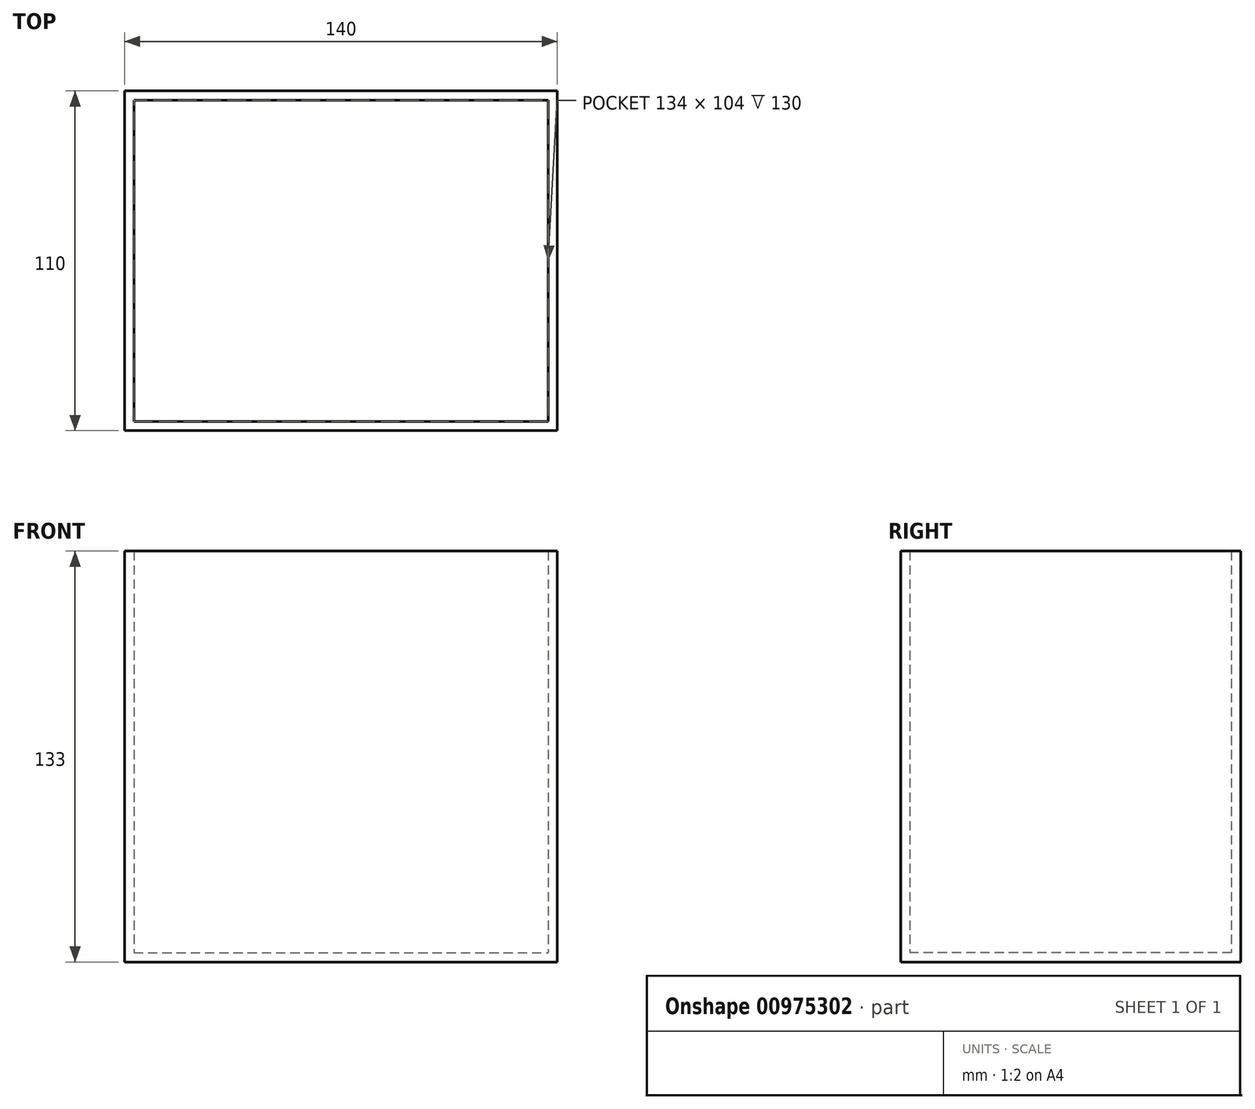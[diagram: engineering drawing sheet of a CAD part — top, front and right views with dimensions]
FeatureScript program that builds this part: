
annotation { "Feature Type Name" : "Feature", "Feature Type Description" : "" }
export const myFeature = defineFeature(function(context is Context, id is Id, definition is map)
    precondition{}
    {
        {
            var Q0;
            Q0=qCreatedBy(makeId("Top.planeOp"),FACE);
            var sketch = newSketch(context, id + "F0", { "sketchPlane" : qUnion([Q0])});
            skLineSegment(sketch, "E0.bottom", {"start": v(-70, 55) * mm, "end": v(70, 55) * mm});
            skLineSegment(sketch, "E0.top", {"start": v(-70, -55) * mm, "end": v(70, -55) * mm});
            skLineSegment(sketch, "E0.left", {"start": v(-70, 55) * mm, "end": v(-70, -55) * mm});
            skLineSegment(sketch, "E0.right", {"start": v(70, 55) * mm, "end": v(70, -55) * mm});
            skLineSegment(sketch, "E1.bottom", {"start": v(-67, 52) * mm, "end": v(67, 52) * mm});
            skLineSegment(sketch, "E1.top", {"start": v(-67, -52) * mm, "end": v(67, -52) * mm});
            skLineSegment(sketch, "E1.left", {"start": v(-67, 52) * mm, "end": v(-67, -52) * mm});
            skLineSegment(sketch, "E1.right", {"start": v(67, 52) * mm, "end": v(67, -52) * mm});
            skSolve(sketch);
        }
        {
            var Q0;
            Q0=makeQuery(id+"F0.imprint","IMPRINT",FACE,{"disambiguationData":[TD([[makeQuery(id+"F0.imprint","IMPRINT",EDGE,{"derivedFrom":sQuery(id+"F0.wireOp",EDGE,"E0.bottom")}),-1.0]])]});
            extrude(context, id + "F1", {"entities" : qUnion([Q0]), "depth" : 130 * mm, "offsetDistance" : 25 * mm});
        }
        {
            var Q0;
            Q0=qCreatedBy(makeId("Top.planeOp"),FACE);
            var sketch = newSketch(context, id + "F2", { "sketchPlane" : qUnion([Q0])});
            skLineSegment(sketch, "E2.0", {"start": v(-70, -55) * mm, "end": v(70, -55) * mm});
            skLineSegment(sketch, "E3.0", {"start": v(-70, 55) * mm, "end": v(-70, -55) * mm});
            skLineSegment(sketch, "E4.0", {"start": v(70, 55) * mm, "end": v(70, -55) * mm});
            skLineSegment(sketch, "E5.0", {"start": v(-70, 55) * mm, "end": v(70, 55) * mm});
            skSolve(sketch);
        }
        {
            var Q0;
            Q0 = qSketchRegion(id + "F2", true);
            extrude(context, id + "F3", {"entities" : qUnion([Q0]), "operationType" : NewBodyOperationType.ADD, "oppositeDirection" : true, "depth" : 3 * mm, "offsetDistance" : 25 * mm});
        }
    });
